# Revit family: Gira_216000
name_source: partatom
category: Elektroinstallationen
revit_build: Autodesk Revit 2017 (Build: 20160225_1515(x64)
units: mm (PartAtom-declared; Revit-internal decimal feet)

## family parameters
Basisbauteil = Fläche
Beim Laden mit Abzugskörper schneiden = Nein
Bemaßung runder Anschluss = Durchmesser verwenden
Beschriftungsausrichtung beibehalten = Nein
Gemeinsam genutzt = Nein
Raumberechnungspunkt = Nein
Teiletyp = Normal

## types (1)
- Rollladenaktor 4f AC 230 V Hand KNX REG
    Andere Bussysteme = ohne
    Anzahl der Ausgänge = 0
    Anzahl der Eingänge = 1
    Anzahl der binären Eingänge = 0
    BIM = https://media.stage.bim.site 8f.rfa
    BIMSITE_PRODUCT_ID = e0d490d711951edfc0e10b13a19cc258dc9395b6
    Bemessungsstrom = 0 A
    Beschreibung = KNX Rollladenaktor 4fach AC 230 V mit Handbetätigung  REG plus Merkmale:  Rollladenaktor mit Handbetätigung und Statusanzeige für jeden Ausgang.  Mit integrierter Busankopplung.  Zum Ansteuern von elektrisch betriebenen Rollläden für Netzspannung AC 230 V (4-kanalig).  Anschluss verschiedener Außenleiter.  Unabhängige Ansteuerung der vier Rollladenausgänge.  Rollladenposition direkt ansteuerbar.  Verhalten bei Busspannungsausfall und -wiederkehr einstellbar.  Rückmeldung der Position. Aktive oder passive (Objekt auslesbar) zyklische Rückmeldefunktionen.  Zuordnungen auf bis zu fünf verschiedene Sicherheitsfunktionen (drei Windalarme, ein Regenalarm, ein Frostalarm), wahlweise mit zyklischer Überwachung.  Baustellenbetrieb: Ausgänge manuell bedienbar ohne Busspannung nur mit der Betriebsspannung.  Hinweise :  VDE-Zulassung gemäß EN 60669-1, EN 60669-2-1.  Montage auf DIN-Hutschiene.
    Blindleistung = Nein
    Breite in Teilungseinheiten = 4
    Busspannung pufferbar = Nein
    Bussystem Funkbus = Nein
    Bussystem KNX = Ja
    Bussystem KNX-Funk = Nein
    Bussystem LON = Nein
    Bussystem Powernet = Nein
    Datenblatt = https://media.stage.bim.site
    Datenblatt 1 = https://media.stage.bim.site
    Funktion Schalten = Nein
    GTIN = 4010337101352
    Geeignet für C-Last = Nein
    HAN = 216000
    Handschaltung = Nein
    HeinzeBIM = https://www.heinze.de
    Hersteller = Gira
    Kosten = 0 $
    LED ansteuern = Nein
    Max. Anzahl der Jalousieausgänge = 4
    Max. Anzahl der Schaltausgänge = 0
    Max. Ausgangsstrom = 0 A
    Max. Schaltleistung [Voltampere] = 0
    Max. Schaltstrom = 0 A
    Mit Busankopplung = Ja
    Mit LED-Anzeige = Nein
    Modulare Erweiterungsmöglichkeit = Nein
    Montageart = REG
    Produktseite = https://media.stage.bim.site
    Schaltstrom ohmsch = 0 A
    Schutzart (IP) = IP20
    Stellgröße schaltend = Nein
    Stellgröße stetig = Nein
    Stromart = AC
    Tarifumschaltung = Nein
    Typname = Rollladenaktor 4f AC 230 V Hand KNX REG
    URL = https://www.gira.de
    Ventilschutzfunktion = Nein
    Verschiedene Phasen anschließbar = Nein
    Vor Ort-/Handbedienung = Ja
    Vorgabe-Ansicht = 1219 mm
    Zulassung nach PTB = Nein

## geometry (parser evidence)
native form markers: Sweep x3
no freeform markers — native parametric forms only
